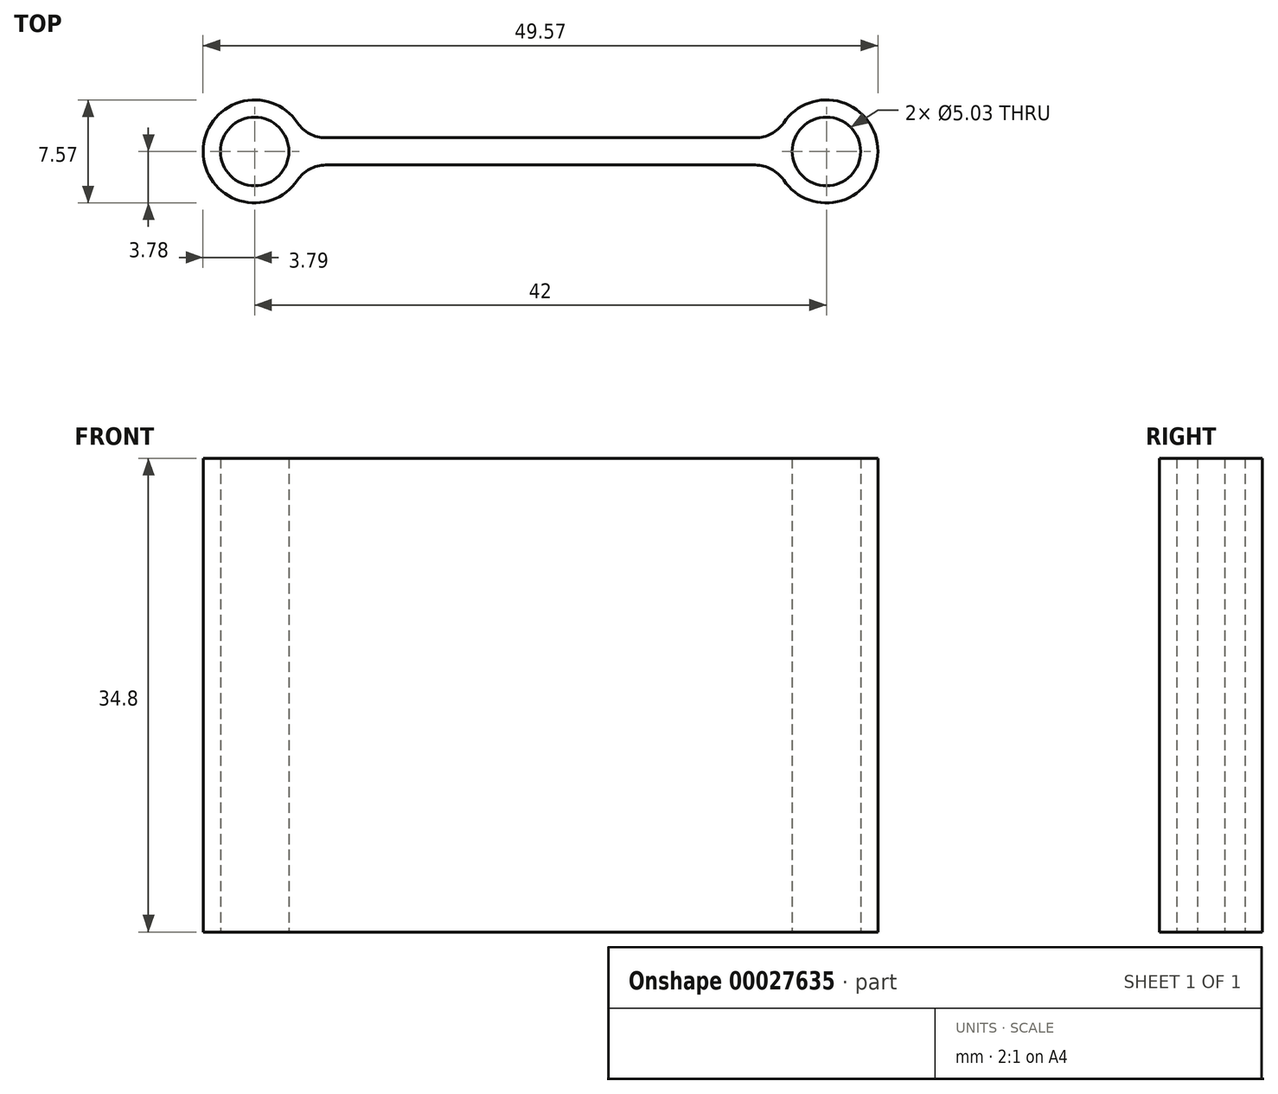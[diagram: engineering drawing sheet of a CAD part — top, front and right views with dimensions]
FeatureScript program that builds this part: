
annotation { "Feature Type Name" : "Feature", "Feature Type Description" : "" }
export const myFeature = defineFeature(function(context is Context, id is Id, definition is map)
    precondition{}
    {
        {
            var Q0;
            Q0=qCreatedBy(makeId("Top.planeOp"),FACE);
            var sketch = newSketch(context, id + "F0", { "sketchPlane" : qUnion([Q0])});
            skCircle(sketch, "E0", {"center": v(-21, 0) * mm, "radius": 2.52 * mm});
            skCircle(sketch, "E1", {"center": v(21, 0) * mm, "radius": 2.52 * mm});
            skLineSegment(sketch, "E2", {"start": v(-15.78, 1) * mm, "end": v(15.78, 1) * mm});
            skLineSegment(sketch, "E3", {"start": v(-15.78, -1) * mm, "end": v(15.78, -1) * mm});
            skArc(sketch, "E4", {"start": v(-17.86, 2.1) * mm, "mid": v(-24.79, 0) * mm, "end": v(-17.86, -2.1) * mm});
            skArc(sketch, "E5", {"start": v(17.86, -2.1) * mm, "mid": v(24.78, 0) * mm, "end": v(17.86, 2.1) * mm});
            skPoint(sketch, "E6.visualSharp", {"position": v(-17.35, 1) * mm});
            skArc(sketch, "E6.filletArc", {"start": v(-17.86, 2.1) * mm, "mid": v(-16.96, 1.3) * mm, "end": v(-15.78, 1) * mm});
            skPoint(sketch, "E7.visualSharp", {"position": v(-17.35, -1) * mm});
            skArc(sketch, "E7.filletArc", {"start": v(-15.78, -1) * mm, "mid": v(-16.96, -1.3) * mm, "end": v(-17.86, -2.1) * mm});
            skPoint(sketch, "E8.visualSharp", {"position": v(17.35, 1) * mm});
            skArc(sketch, "E8.filletArc", {"start": v(15.78, 1) * mm, "mid": v(16.96, 1.3) * mm, "end": v(17.86, 2.1) * mm});
            skPoint(sketch, "E9.visualSharp", {"position": v(17.35, -1) * mm});
            skArc(sketch, "E9.filletArc", {"start": v(17.86, -2.1) * mm, "mid": v(16.96, -1.3) * mm, "end": v(15.78, -1) * mm});
            skSolve(sketch);
        }
        {
            var Q0;
            Q0 = qSketchRegion(id + "F0", true);
            extrude(context, id + "F1", {"entities" : qUnion([Q0]), "depth" : 34.8 * mm});
        }
    });
